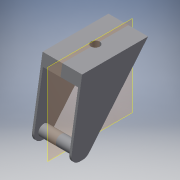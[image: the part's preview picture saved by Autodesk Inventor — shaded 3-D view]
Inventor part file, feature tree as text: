
AUTODESK INVENTOR PART (.ipt)
format: ipt  version: 2019 (Build 230136000, 136)  size: 140,800 bytes
history: native  units: mm
features: extrude x3, sketch x3, other x2, projected_geometry x2
ambient origin geometry x8: Origin, YZ Plane, XZ Plane, XY Plane, X Axis, Y Axis, Z Axis, Center Point
bodies: Body1 (feature_tree)
feature tree (10):
  other  "솔리드1"
  extrude  "돌출1"  Depth=67.5mm
  other  "작업 평면1"
  extrude  "돌출2"  Depth=82.0mm
  extrude  "돌출3"  Depth=30.0mm
  sketch  "스케치1"
  sketch  "스케치2"
  projected_geometry  "투영된 루프1"
  sketch  "스케치3"
  projected_geometry  "투영된 루프2"
